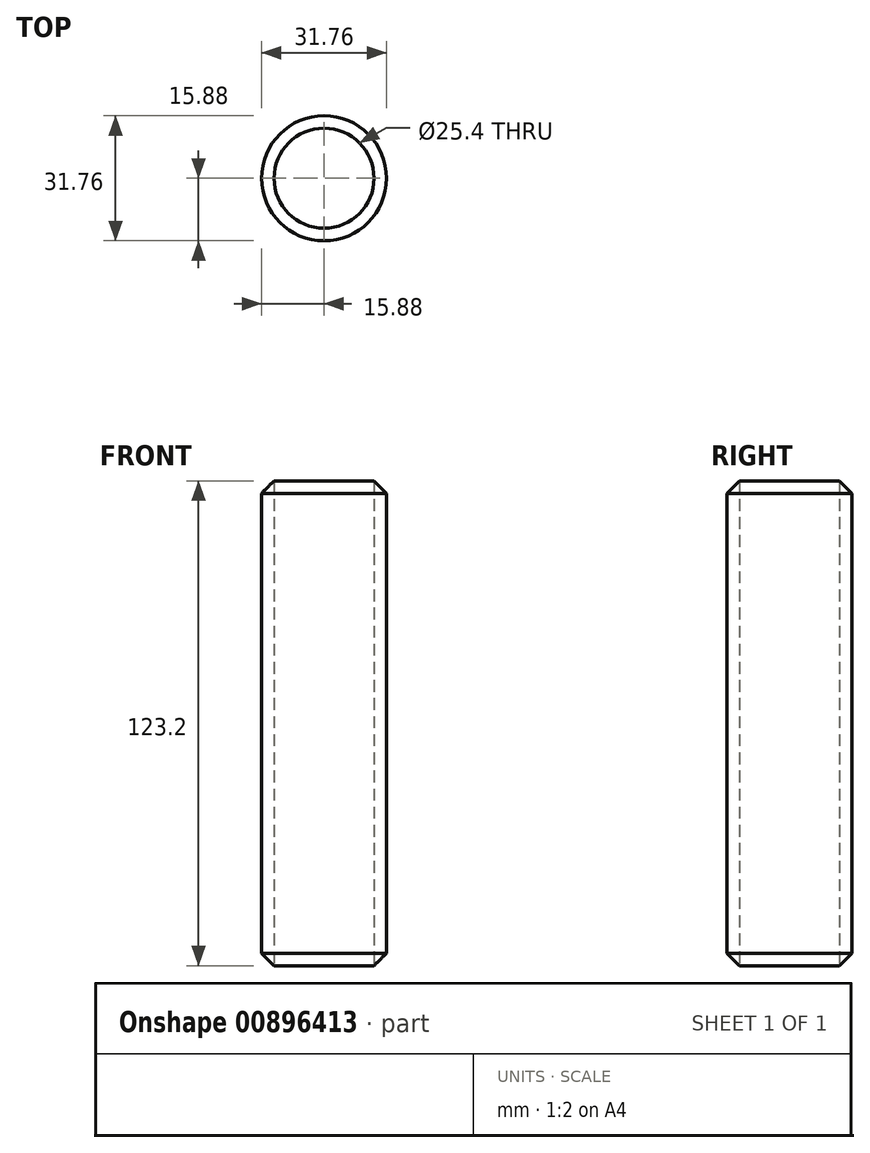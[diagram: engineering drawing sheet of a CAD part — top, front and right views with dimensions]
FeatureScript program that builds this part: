
annotation { "Feature Type Name" : "Feature", "Feature Type Description" : "" }
export const myFeature = defineFeature(function(context is Context, id is Id, definition is map)
    precondition{}
    {
        {
            var Q0;
            Q0=qCreatedBy(makeId("Top.planeOp"),FACE);
            var sketch = newSketch(context, id + "F0", { "sketchPlane" : qUnion([Q0])});
            skCircle(sketch, "E0", {"center": v(0, 0) * mm, "radius": 15.88 * mm});
            skCircle(sketch, "E1", {"center": v(0, 0) * mm, "radius": 12.7 * mm});
            skSolve(sketch);
        }
        {
            var Q0;
            Q0=makeQuery(id+"F0.imprint","IMPRINT",FACE,{"disambiguationData":[TD([[makeQuery(id+"F0.imprint","IMPRINT",EDGE,{"derivedFrom":sQuery(id+"F0.wireOp",EDGE,"E0")}),1.0]])]});
            extrude(context, id + "F1", {"entities" : qUnion([Q0]), "depth" : 127 * mm, "offsetDistance" : 25.4 * mm});
        }
        {
            var Q0;
            Q0=makeQuery(id+"F1.opExtrude","CAP_EDGE",EDGE,{"disambiguationData":[OSD([sQuery(id+"F0.wireOp",EDGE,"E0")])],"isStart":true});
            var Q1;
            Q1=makeQuery(id+"F1.opExtrude","SWEPT_FACE",FACE,{"disambiguationData":[OSD([sQuery(id+"F0.wireOp",EDGE,"E0")])]});
            chamfer(context, id + "F2", {"entities" : qUnion([Q0, Q1]), "width" : 5.08 * mm, "tangentPropagation" : true});
        }
    });
